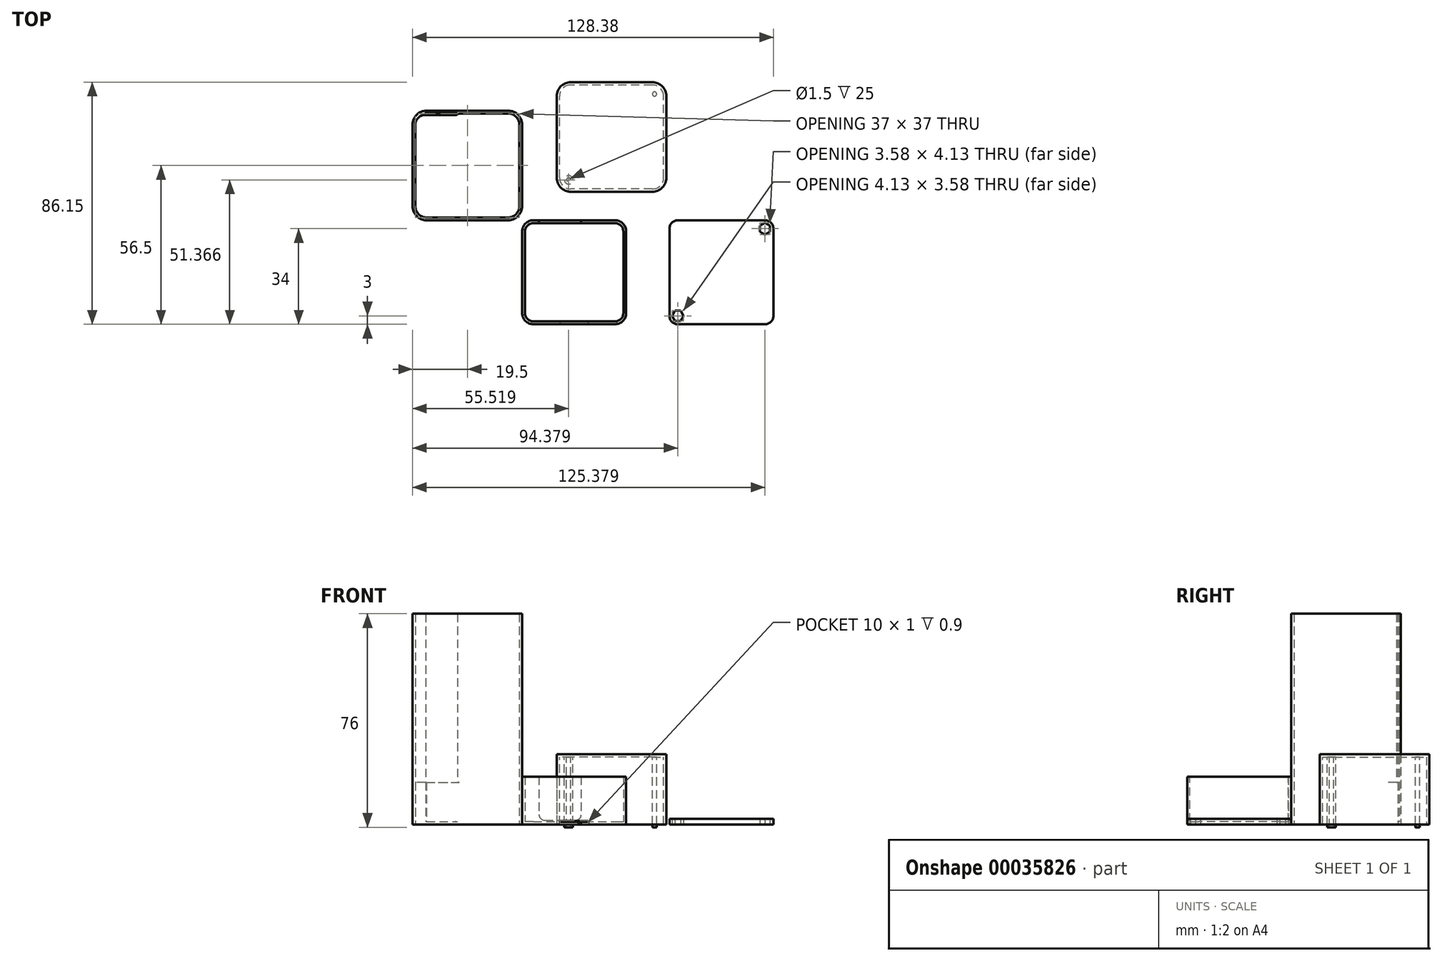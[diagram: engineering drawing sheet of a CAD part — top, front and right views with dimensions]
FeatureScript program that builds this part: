
annotation { "Feature Type Name" : "Feature", "Feature Type Description" : "" }
export const myFeature = defineFeature(function(context is Context, id is Id, definition is map)
    precondition{}
    {
        {
            var Q0;
            Q0=qCreatedBy(makeId("Top.planeOp"),FACE);
            var sketch = newSketch(context, id + "F0", { "sketchPlane" : qUnion([Q0])});
            skLineSegment(sketch, "E0.bottom", {"start": v(4, 0) * mm, "end": v(33, 0) * mm});
            skLineSegment(sketch, "E0.top", {"start": v(4, -37) * mm, "end": v(33, -37) * mm});
            skLineSegment(sketch, "E0.left", {"start": v(0, -4) * mm, "end": v(0, -33) * mm});
            skLineSegment(sketch, "E0.right", {"start": v(37, -4) * mm, "end": v(37, -33) * mm});
            skPoint(sketch, "E1.visualSharp", {"position": v(37, 0) * mm});
            skArc(sketch, "E1.filletArc", {"start": v(37, -4) * mm, "mid": v(35.83, -1.17) * mm, "end": v(33, 0) * mm});
            skPoint(sketch, "E2.visualSharp", {"position": v(37, -37) * mm});
            skArc(sketch, "E2.filletArc", {"start": v(33, -37) * mm, "mid": v(35.83, -35.83) * mm, "end": v(37, -33) * mm});
            skPoint(sketch, "E3.visualSharp", {"position": v(0, -37) * mm});
            skArc(sketch, "E3.filletArc", {"start": v(0, -33) * mm, "mid": v(1.17, -35.83) * mm, "end": v(4, -37) * mm});
            skPoint(sketch, "E4.visualSharp", {"position": v(0, 0) * mm});
            skArc(sketch, "E4.filletArc", {"start": v(4, 0) * mm, "mid": v(1.17, -1.17) * mm, "end": v(0, -4) * mm});
            skSolve(sketch);
        }
        {
            var Q0;
            Q0=makeQuery(id+"F0.imprint","IMPRINT",FACE,{"disambiguationData":[TD([[makeQuery(id+"F0.imprint","IMPRINT",EDGE,{"derivedFrom":sQuery(id+"F0.wireOp",EDGE,"E0.bottom")}),-1.0]])]});
            extrude(context, id + "F1", {"entities" : qUnion([Q0]), "depth" : 17 * mm});
        }
        {
            var Q0;
            Q0=makeQuery(id+"F1.opExtrude","CAP_FACE",FACE,{"disambiguationData":[OSD([sQuery(id+"F0.wireOp",EDGE,"E0.bottom"),sQuery(id+"F0.wireOp",EDGE,"E0.top"),sQuery(id+"F0.wireOp",EDGE,"E0.left"),sQuery(id+"F0.wireOp",EDGE,"E0.right")])],"isStart":false});
            shell(context, id + "F2", {"entities" : qUnion([Q0]), "thickness" : 1 * mm});
        }
        {
            var Q0;
            Q0=makeQuery(id+"F1.opExtrude","SWEPT_FACE",FACE,{"disambiguationData":[OSD([sQuery(id+"F0.wireOp",EDGE,"E0.bottom")])]});
            var sketch = newSketch(context, id + "F3", { "sketchPlane" : qUnion([Q0])});
            skLineSegment(sketch, "E5.top", {"start": v(-8, 1.5) * mm, "end": v(-19, 1.5) * mm});
            skLineSegment(sketch, "E5.right", {"start": v(-21, 17) * mm, "end": v(-21, 3.5) * mm});
            skArc(sketch, "E6.filletArc", {"start": v(-21, 3.5) * mm, "mid": v(-20.41, 2.09) * mm, "end": v(-19, 1.5) * mm});
            skLineSegment(sketch, "E7", {"start": v(-6, 17) * mm, "end": v(-6, 3.5) * mm});
            skArc(sketch, "E8.filletArc", {"start": v(-8, 1.5) * mm, "mid": v(-6.59, 2.09) * mm, "end": v(-6, 3.5) * mm});
            skLineSegment(sketch, "E9", {"start": v(-6, 17) * mm, "end": v(-21, 17) * mm});
            skLineSegment(sketch, "E10.0.0", {"start": v(-33, 0) * mm, "end": v(-4, 0) * mm});
            skLineSegment(sketch, "E10.0.1", {"start": v(-4, 0) * mm, "end": v(-4, 17) * mm});
            skLineSegment(sketch, "E10.0.2", {"start": v(-4, 17) * mm, "end": v(-33, 17) * mm});
            skLineSegment(sketch, "E10.0.3", {"start": v(-33, 17) * mm, "end": v(-33, 0) * mm});
            skLineSegment(sketch, "E11.bottom", {"start": v(-23.5, 1.2) * mm, "end": v(-13.5, 1.2) * mm});
            skLineSegment(sketch, "E11.top", {"start": v(-23.5, 0.2) * mm, "end": v(-13.5, 0.2) * mm});
            skLineSegment(sketch, "E11.left", {"start": v(-23.5, 1.2) * mm, "end": v(-23.5, 0.2) * mm});
            skLineSegment(sketch, "E11.right", {"start": v(-13.5, 1.2) * mm, "end": v(-13.5, 0.2) * mm});
            skSolve(sketch);
        }
        {
            var Q0;
            Q0=makeQuery(id+"F3.imprint","IMPRINT",FACE,{"disambiguationData":[TD([[makeQuery(id+"F3.imprint","IMPRINT",EDGE,{"derivedFrom":sQuery(id+"F3.wireOp",EDGE,"E5.top")}),-1.0]])]});
            extrude(context, id + "F4", {"entities" : qUnion([Q0]), "operationType" : NewBodyOperationType.REMOVE, "oppositeDirection" : true, "depth" : 2 * mm});
        }
        {
            var Q0;
            Q0=makeQuery(id+"F1.opExtrude","SWEPT_FACE",FACE,{"disambiguationData":[OSD([sQuery(id+"F0.wireOp",EDGE,"E0.top")])]});
            var sketch = newSketch(context, id + "F5", { "sketchPlane" : qUnion([Q0])});
            skLineSegment(sketch, "E12.bottom", {"start": v(13.5, 1.3) * mm, "end": v(23.5, 1.3) * mm});
            skLineSegment(sketch, "E12.left", {"start": v(13.5, 1.3) * mm, "end": v(13.5, 0.3) * mm});
            skLineSegment(sketch, "E12.right", {"start": v(23.5, 1.3) * mm, "end": v(23.5, 0.3) * mm});
            skLineSegment(sketch, "E12.top", {"start": v(13.5, 0.3) * mm, "end": v(23.5, 0.3) * mm});
            skSolve(sketch);
        }
        {
            var Q0;
            Q0=makeQuery(id+"F5.imprint","IMPRINT",FACE,{"disambiguationData":[TD([[makeQuery(id+"F5.imprint","IMPRINT",EDGE,{"derivedFrom":sQuery(id+"F5.wireOp",EDGE,"E12.bottom")}),-1.0]])]});
            extrude(context, id + "F6", {"entities" : qUnion([Q0]), "operationType" : NewBodyOperationType.REMOVE, "oppositeDirection" : true, "depth" : .9 * mm});
        }
        {
            var Q0;
            Q0=qCreatedBy(makeId("Top.planeOp"),FACE);
            var sketch = newSketch(context, id + "F7", { "sketchPlane" : qUnion([Q0])});
            skLineSegment(sketch, "E13.bottom", {"start": v(-5, 0) * mm, "end": v(-34, 0) * mm});
            skLineSegment(sketch, "E13.top", {"start": v(-5, 39) * mm, "end": v(-34, 39) * mm});
            skLineSegment(sketch, "E13.left", {"start": v(0, 5) * mm, "end": v(0, 34) * mm});
            skLineSegment(sketch, "E13.right", {"start": v(-39, 5) * mm, "end": v(-39, 34) * mm});
            skPoint(sketch, "E14.visualSharp", {"position": v(-39, 39) * mm});
            skArc(sketch, "E14.filletArc", {"start": v(-34, 39) * mm, "mid": v(-37.54, 37.54) * mm, "end": v(-39, 34) * mm});
            skPoint(sketch, "E15.visualSharp", {"position": v(0, 39) * mm});
            skArc(sketch, "E15.filletArc", {"start": v(0, 34) * mm, "mid": v(-1.46, 37.54) * mm, "end": v(-5, 39) * mm});
            skPoint(sketch, "E16.visualSharp", {"position": v(0, 0) * mm});
            skArc(sketch, "E16.filletArc", {"start": v(-5, 0) * mm, "mid": v(-1.46, 1.46) * mm, "end": v(0, 5) * mm});
            skPoint(sketch, "E17.visualSharp", {"position": v(-39, 0) * mm});
            skArc(sketch, "E17.filletArc", {"start": v(-39, 5) * mm, "mid": v(-37.54, 1.46) * mm, "end": v(-34, 0) * mm});
            skLineSegment(sketch, "E18", {"start": v(-34, 38) * mm, "end": v(-24.04, 38) * mm});
            skLineSegment(sketch, "E19", {"start": v(-34.5, 37.5) * mm, "end": v(-23.4, 37.5) * mm});
            skLineSegment(sketch, "E20", {"start": v(-34, 38.5) * mm, "end": v(-24.04, 38.5) * mm});
            skLineSegment(sketch, "E21", {"start": v(-22.37, 38) * mm, "end": v(-5, 38) * mm});
            skLineSegment(sketch, "E22", {"start": v(-1, 34) * mm, "end": v(-1, 5) * mm});
            skArc(sketch, "E23.filletArc", {"start": v(-1, 34) * mm, "mid": v(-2.17, 36.83) * mm, "end": v(-5, 38) * mm});
            skLineSegment(sketch, "E24", {"start": v(-34, 1) * mm, "end": v(-5, 1) * mm});
            skLineSegment(sketch, "E25", {"start": v(-38, 5) * mm, "end": v(-38, 34) * mm});
            skArc(sketch, "E26.filletArc", {"start": v(-38, 5) * mm, "mid": v(-36.83, 2.17) * mm, "end": v(-34, 1) * mm});
            skArc(sketch, "E27.filletArc", {"start": v(-5, 1) * mm, "mid": v(-2.17, 2.17) * mm, "end": v(-1, 5) * mm});
            skArc(sketch, "E28.filletArc", {"start": v(-34.5, 37.5) * mm, "mid": v(-36.97, 36.47) * mm, "end": v(-38, 34) * mm});
            skArc(sketch, "E29", {"start": v(-24.04, 38) * mm, "mid": v(-23.8, 38.25) * mm, "end": v(-24.04, 38.5) * mm});
            skLineSegment(sketch, "E30", {"start": v(-23.12, 37.59) * mm, "end": v(-22.66, 37.91) * mm});
            skPoint(sketch, "E31.visualSharp", {"position": v(-22.53, 38) * mm});
            skArc(sketch, "E31.filletArc", {"start": v(-22.37, 38) * mm, "mid": v(-22.52, 37.98) * mm, "end": v(-22.66, 37.91) * mm});
            skPoint(sketch, "E32.visualSharp", {"position": v(-23.25, 37.5) * mm});
            skArc(sketch, "E32.filletArc", {"start": v(-23.4, 37.5) * mm, "mid": v(-23.26, 37.52) * mm, "end": v(-23.12, 37.59) * mm});
            skLineSegment(sketch, "E33", {"start": v(-24.04, 38.5) * mm, "end": v(-23.9, 38.5) * mm});
            skLineSegment(sketch, "E34", {"start": v(-23.56, 38.37) * mm, "end": v(-23.3, 38.13) * mm});
            skLineSegment(sketch, "E35", {"start": v(-22.97, 38) * mm, "end": v(-22.37, 38) * mm});
            skPoint(sketch, "E36.visualSharp", {"position": v(-23.16, 38) * mm});
            skArc(sketch, "E36.filletArc", {"start": v(-23.3, 38.13) * mm, "mid": v(-23.15, 38.03) * mm, "end": v(-22.97, 38) * mm});
            skPoint(sketch, "E37.visualSharp", {"position": v(-23.7, 38.5) * mm});
            skArc(sketch, "E37.filletArc", {"start": v(-23.56, 38.37) * mm, "mid": v(-23.72, 38.47) * mm, "end": v(-23.9, 38.5) * mm});
            skLineSegment(sketch, "E38", {"start": v(-24.04, 38) * mm, "end": v(-22.97, 38) * mm});
            skLineSegment(sketch, "E39", {"start": v(-38, 34) * mm, "end": v(-38, 34) * mm});
            skArc(sketch, "E40.filletArc", {"start": v(-34, 38) * mm, "mid": v(-36.83, 36.83) * mm, "end": v(-38, 34) * mm});
            skArc(sketch, "E41", {"start": v(-34, 38.5) * mm, "mid": v(-34.25, 38.25) * mm, "end": v(-34, 38) * mm});
            skSolve(sketch);
        }
        {
            var Q0;
            Q0=makeQuery(id+"F7.imprint","IMPRINT",FACE,{"disambiguationData":[TD([[makeQuery(id+"F7.imprint","IMPRINT",EDGE,{"derivedFrom":sQuery(id+"F7.wireOp",EDGE,"E13.bottom")}),-1.0]])]});
            var Q1;
            Q1=makeQuery(id+"F7.imprint","IMPRINT",FACE,{"disambiguationData":[TD([[makeQuery(id+"F7.imprint","IMPRINT",EDGE,{"derivedFrom":sQuery(id+"F7.wireOp",EDGE,"E18")}),-1.0]])]});
            extrude(context, id + "F8", {"entities" : qUnion([Q0, Q1]), "depth" : 25 * mm * 3});
        }
        {
            var Q0;
            Q0=makeQuery(id+"F7.imprint","IMPRINT",FACE,{"disambiguationData":[TD([[makeQuery(id+"F7.imprint","IMPRINT",EDGE,{"derivedFrom":sQuery(id+"F7.wireOp",EDGE,"E18")}),-1.0]])]});
            extrude(context, id + "F9", {"entities" : qUnion([Q0]), "operationType" : NewBodyOperationType.REMOVE, "depth" : 15 * mm});
        }
        {
            var Q0;
            Q0=makeQuery(id+"F7.imprint","IMPRINT",FACE,{"disambiguationData":[TD([[makeQuery(id+"F7.imprint","IMPRINT",EDGE,{"derivedFrom":sQuery(id+"F7.wireOp",EDGE,"E18")}),1.0]])]});
            var Q1;
            Q1=makeQuery(id+"F7.imprint","IMPRINT",FACE,{"disambiguationData":[TD([[makeQuery(id+"F7.imprint","IMPRINT",EDGE,{"derivedFrom":sQuery(id+"F7.wireOp",EDGE,"E29")}),-1.0]])]});
            extrude(context, id + "F10", {"entities" : qUnion([Q0, Q1]), "operationType" : NewBodyOperationType.ADD, "depth" : 1 * mm});
        }
        {
            var Q0;
            Q0=qCreatedBy(makeId("Top.planeOp"),FACE);
            var sketch = newSketch(context, id + "F11", { "sketchPlane" : qUnion([Q0])});
            skLineSegment(sketch, "E42.left", {"start": v(51.3, 15.15) * mm, "end": v(51.3, 44.15) * mm});
            skPoint(sketch, "E43.visualSharp", {"position": v(51.3, 49.15) * mm});
            skPoint(sketch, "E44.visualSharp", {"position": v(12.3, 49.15) * mm});
            skPoint(sketch, "E45.visualSharp", {"position": v(12.3, 10.15) * mm});
            skLineSegment(sketch, "E42.right", {"start": v(12.3, 15.15) * mm, "end": v(12.3, 44.15) * mm});
            skLineSegment(sketch, "E42.top", {"start": v(46.3, 49.15) * mm, "end": v(36.66, 49.15) * mm});
            skPoint(sketch, "E46.visualSharp", {"position": v(51.3, 10.15) * mm});
            skLineSegment(sketch, "E42.bottom", {"start": v(46.3, 10.15) * mm, "end": v(17.3, 10.15) * mm});
            skLineSegment(sketch, "E47", {"start": v(17.3, 49.15) * mm, "end": v(36.53, 49.15) * mm});
            skArc(sketch, "E45.filletArc", {"start": v(12.3, 15.15) * mm, "mid": v(13.76, 11.61) * mm, "end": v(17.3, 10.15) * mm});
            skArc(sketch, "E46.filletArc", {"start": v(46.3, 10.15) * mm, "mid": v(49.84, 11.61) * mm, "end": v(51.3, 15.15) * mm});
            skArc(sketch, "E43.filletArc", {"start": v(51.3, 44.15) * mm, "mid": v(49.84, 47.68) * mm, "end": v(46.3, 49.15) * mm});
            skArc(sketch, "E44.filletArc", {"start": v(17.3, 49.15) * mm, "mid": v(13.76, 47.68) * mm, "end": v(12.3, 44.15) * mm});
            skLineSegment(sketch, "E48", {"start": v(36.53, 49.15) * mm, "end": v(36.66, 49.15) * mm});
            skSolve(sketch);
        }
        {
            var Q0;
            Q0=qSketchRegion(id+"F11",true);
            extrude(context, id + "F12", {"entities" : qUnion([Q0]), "depth" : 25 * mm});
        }
        {
            var Q0;
            Q0=makeQuery(id+"F12.opExtrude","CAP_FACE",FACE,{"disambiguationData":[OSD([sQuery(id+"F11.wireOp",EDGE,"E42.left"),sQuery(id+"F11.wireOp",EDGE,"E42.right"),sQuery(id+"F11.wireOp",EDGE,"E42.top"),sQuery(id+"F11.wireOp",EDGE,"E42.bottom"),sQuery(id+"F11.wireOp",EDGE,"E47"),sQuery(id+"F11.wireOp",EDGE,"E45.filletArc"),sQuery(id+"F11.wireOp",EDGE,"E46.filletArc"),sQuery(id+"F11.wireOp",EDGE,"E43.filletArc"),sQuery(id+"F11.wireOp",EDGE,"E44.filletArc"),sQuery(id+"F11.wireOp",EDGE,"E48")])],"isStart":true});
            shell(context, id + "F13", {"entities" : qUnion([Q0]), "thickness" : 1 * mm});
        }
        {
            var Q0;
            Q0=makeQuery(id+"F13.opShell","OFFSET_FACE",FACE,{"disambiguationData":[OSD([sQuery(id+"F11.wireOp",EDGE,"E42.left"),sQuery(id+"F11.wireOp",EDGE,"E42.right"),sQuery(id+"F11.wireOp",EDGE,"E42.top"),sQuery(id+"F11.wireOp",EDGE,"E42.bottom"),sQuery(id+"F11.wireOp",EDGE,"E47"),sQuery(id+"F11.wireOp",EDGE,"E45.filletArc"),sQuery(id+"F11.wireOp",EDGE,"E46.filletArc"),sQuery(id+"F11.wireOp",EDGE,"E43.filletArc"),sQuery(id+"F11.wireOp",EDGE,"E44.filletArc"),sQuery(id+"F11.wireOp",EDGE,"E48")])]});
            var sketch = newSketch(context, id + "F14", { "sketchPlane" : qUnion([Q0])});
            skLineSegment(sketch, "E49", {"start": v(49.13, -12.32) * mm, "end": v(14.47, -46.98) * mm});
            skCircle(sketch, "E50", {"center": v(16.52, -14.37) * mm, "radius": 0.75 * mm});
            skPoint(sketch, "E51.start.orphan", {"position": v(14.47, -12.32) * mm});
            skPoint(sketch, "E52.trimOffspring.end.orphan", {"position": v(49.13, -46.98) * mm});
            skCircle(sketch, "E53.MirrorC", {"center": v(47.08, -44.93) * mm, "radius": 0.75 * mm});
            skCircle(sketch, "E54", {"center": v(16.52, -14.37) * mm, "radius": 1.5 * mm});
            skCircle(sketch, "E55.MirrorC", {"center": v(47.08, -44.93) * mm, "radius": 1.5 * mm});
            skSolve(sketch);
        }
        {
            var Q0;
            Q0=makeQuery(id+"F14.imprint","IMPRINT",FACE,{"disambiguationData":[TD([[makeQuery(id+"F14.imprint","IMPRINT",EDGE,{"derivedFrom":sQuery(id+"F14.wireOp",EDGE,"E50")}),-1.0]])]});
            var Q1;
            Q1=makeQuery(id+"F14.imprint","IMPRINT",FACE,{"disambiguationData":[TD([[makeQuery(id+"F14.imprint","IMPRINT",EDGE,{"derivedFrom":sQuery(id+"F14.wireOp",EDGE,"E53.MirrorC")}),1.0]])]});
            extrude(context, id + "F15", {"entities" : qUnion([Q0, Q1]), "operationType" : NewBodyOperationType.ADD, "depth" : 25 * mm});
        }
        {
            var Q0;
            Q0=qCreatedBy(makeId("Top.planeOp"),FACE);
            var sketch = newSketch(context, id + "F16", { "sketchPlane" : qUnion([Q0])});
            skLineSegment(sketch, "E56.bottom", {"start": v(55.38, 0) * mm, "end": v(86.38, 0) * mm});
            skLineSegment(sketch, "E56.top", {"start": v(55.38, -37) * mm, "end": v(86.38, -37) * mm});
            skLineSegment(sketch, "E56.left", {"start": v(52.38, -3) * mm, "end": v(52.38, -34) * mm});
            skLineSegment(sketch, "E56.right", {"start": v(89.38, -3) * mm, "end": v(89.38, -34) * mm});
            skPoint(sketch, "E57.visualSharp", {"position": v(52.38, 0) * mm});
            skArc(sketch, "E57.filletArc", {"start": v(55.38, 0) * mm, "mid": v(53.26, -0.88) * mm, "end": v(52.38, -3) * mm});
            skPoint(sketch, "E58.visualSharp", {"position": v(89.38, 0) * mm});
            skArc(sketch, "E58.filletArc", {"start": v(89.38, -3) * mm, "mid": v(88.5, -0.88) * mm, "end": v(86.38, 0) * mm});
            skPoint(sketch, "E59.visualSharp", {"position": v(89.38, -37) * mm});
            skArc(sketch, "E59.filletArc", {"start": v(86.38, -37) * mm, "mid": v(88.5, -36.12) * mm, "end": v(89.38, -34) * mm});
            skPoint(sketch, "E60.visualSharp", {"position": v(52.38, -37) * mm});
            skArc(sketch, "E60.filletArc", {"start": v(52.38, -34) * mm, "mid": v(53.26, -36.12) * mm, "end": v(55.38, -37) * mm});
            skLineSegment(sketch, "E61", {"start": v(86.38, -34) * mm, "end": v(55.38, -3) * mm});
            skLineSegment(sketch, "E62", {"start": v(55.38, -34) * mm, "end": v(86.38, -3) * mm});
            skCircle(sketch, "E63.cCircle", {"center": v(55.38, -34) * mm, "radius": 1.79 * mm, "construction": true});
            skLineSegment(sketch, "E63.0", {"start": v(54.35, -32.21) * mm, "end": v(56.41, -32.21) * mm});
            skLineSegment(sketch, "E63.1", {"start": v(56.41, -32.21) * mm, "end": v(57.44, -34) * mm});
            skLineSegment(sketch, "E63.2", {"start": v(57.44, -34) * mm, "end": v(56.41, -35.79) * mm});
            skLineSegment(sketch, "E63.3", {"start": v(56.41, -35.79) * mm, "end": v(54.35, -35.79) * mm});
            skLineSegment(sketch, "E63.4", {"start": v(54.35, -35.79) * mm, "end": v(53.31, -34) * mm});
            skLineSegment(sketch, "E63.5", {"start": v(53.31, -34) * mm, "end": v(54.35, -32.21) * mm});
            skPoint(sketch, "E63.0.midPoint", {"position": v(55.38, -32.21) * mm});
            skLineSegment(sketch, "E64.MirrorCS", {"start": v(86.38, -5.06) * mm, "end": v(88.17, -4.03) * mm});
            skLineSegment(sketch, "E65.MirrorCS", {"start": v(88.17, -4.03) * mm, "end": v(88.17, -1.97) * mm});
            skLineSegment(sketch, "E66.MirrorCS", {"start": v(88.17, -1.97) * mm, "end": v(86.38, -0.94) * mm});
            skLineSegment(sketch, "E67.MirrorCS", {"start": v(86.38, -0.94) * mm, "end": v(84.6, -1.97) * mm});
            skLineSegment(sketch, "E68.MirrorCS", {"start": v(84.6, -1.97) * mm, "end": v(84.6, -4.03) * mm});
            skLineSegment(sketch, "E69.MirrorCS", {"start": v(84.6, -4.03) * mm, "end": v(86.38, -5.06) * mm});
            skSolve(sketch);
        }
        {
            var Q0;
            Q0=makeQuery(id+"F16.imprint","IMPRINT",FACE,{"disambiguationData":[TD([[makeQuery(id+"F16.imprint","IMPRINT",EDGE,{"derivedFrom":sQuery(id+"F16.wireOp",EDGE,"E56.bottom")}),-1.0]])]});
            extrude(context, id + "F17", {"entities" : qUnion([Q0]), "depth" : 2 * mm});
        }
    });
